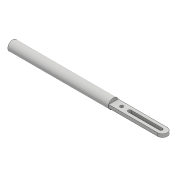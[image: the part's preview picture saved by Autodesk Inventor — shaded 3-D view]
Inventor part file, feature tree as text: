
AUTODESK INVENTOR PART (.ipt)
format: ipt  version: 2017 (Build 210142000, 142)  size: 113,152 bytes
history: native  units: mm
features: extrude x3, sketch x3, plane x1, hole x1
ambient origin geometry x8: Origin, YZ Plane, XZ Plane, XY Plane, X Axis, Y Axis, Z Axis, Center Point
bodies: Solid1 (feature_tree)
feature tree (8):
  extrude  "Extrusion1"  Depth=10.0mm
  plane  "Work Plane1"
  extrude  "Extrusion2"  Depth=20.0mm
  extrude  "Extrusion3"  [1 undecoded]
  hole  "Hole1"  [1 undecoded]
  sketch  "Sketch1"  dims[d0=100.0mm d1=10.0mm]
  sketch  "Sketch2"  dims[d3=20.0mm d6=585.0mm]
  sketch  "Sketch3"  dims[d7=10.0mm d8=0.0mm d9=-151.0mm d10=320.0mm d11=0.0mm d12=169.0mm d13=0.0mm d14=10.0mm d15=10.0mm d16=20.0mm d17=6.0mm d18=4.0mm d19=2.0mm d20=90.0deg d21=305.0mm d22=20.594885mm]
note: 2 required parameter values undecoded (feature->parameter linkage not recoverable at this tier; creation-order binding heuristic only, values carry confidence <= 0.55)
